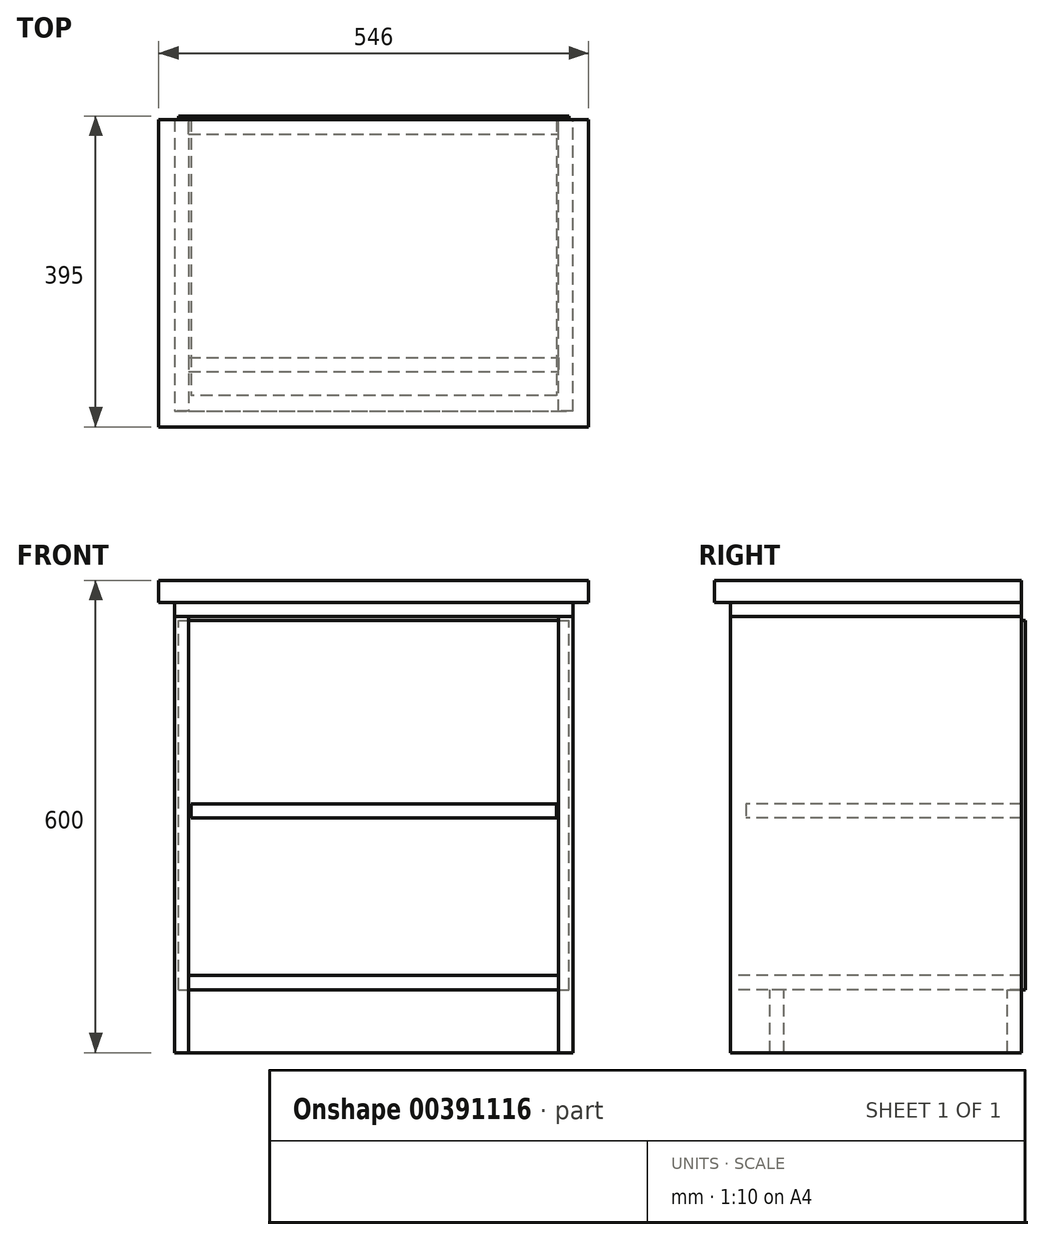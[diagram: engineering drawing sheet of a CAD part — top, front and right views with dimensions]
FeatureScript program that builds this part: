
annotation { "Feature Type Name" : "Feature", "Feature Type Description" : "" }
export const myFeature = defineFeature(function(context is Context, id is Id, definition is map)
    precondition{}
    {
        {
            assignVariable(context, id + "F0", {"name" : "ThickWood", "anyValue" : 28 * mm});
        }
        {
            assignVariable(context, id + "F1", {"name" : "WoodThickness", "anyValue" : 18 * mm});
        }
        {
            var Q0;
            Q0=qCreatedBy(makeId("Right.planeOp"),FACE);
            var sketch = newSketch(context, id + "F2", { "sketchPlane" : qUnion([Q0])});
            skLineSegment(sketch, "E0.bottom", {"start": v(0, 0) * mm, "end": v(-370, 0) * mm});
            skLineSegment(sketch, "E0.top", {"start": v(0, 554) * mm, "end": v(-370, 554) * mm});
            skLineSegment(sketch, "E0.left", {"start": v(0, 0) * mm, "end": v(0, 554) * mm});
            skLineSegment(sketch, "E0.right", {"start": v(-370, 0) * mm, "end": v(-370, 554) * mm});
            skSolve(sketch);
        }
        {
            var Q0;
            Q0=makeQuery(id+"F2.imprint","IMPRINT",FACE,{"disambiguationData":[TD([[makeQuery(id+"F2.imprint","IMPRINT",EDGE,{"derivedFrom":sQuery(id+"F2.wireOp",EDGE,"E0.bottom")}),-1.0]])]});
            extrude(context, id + "F3", {"entities" : qUnion([Q0]), "depth" : getVariable(context, 'WoodThickness')});
        }
        {
            var Q0;
            Q0=makeQuery(id+"F3.opExtrude","CAP_FACE",FACE,{"disambiguationData":[OSD([sQuery(id+"F2.wireOp",EDGE,"E0.bottom"),sQuery(id+"F2.wireOp",EDGE,"E0.top"),sQuery(id+"F2.wireOp",EDGE,"E0.left"),sQuery(id+"F2.wireOp",EDGE,"E0.right")])],"isStart":false});
            cPlane(context, id + "F4", {"entities" : qUnion([Q0]), "cplaneType" : CPlaneType.OFFSET, "offset" : 470 * mm, "width" : 150 * mm, "height" : 150 * mm});
        }
        {
            var Q0;
            Q0=qCreatedBy(id+"F4.planeOp",FACE);
            var sketch = newSketch(context, id + "F5", { "sketchPlane" : qUnion([Q0])});
            skLineSegment(sketch, "E1.bottom", {"start": v(-370, 554) * mm, "end": v(0, 554) * mm});
            skLineSegment(sketch, "E1.top", {"start": v(-370, 0) * mm, "end": v(0, 0) * mm});
            skLineSegment(sketch, "E1.left", {"start": v(-370, 554) * mm, "end": v(-370, 0) * mm});
            skLineSegment(sketch, "E1.right", {"start": v(0, 554) * mm, "end": v(0, 0) * mm});
            skSolve(sketch);
        }
        {
            var Q0;
            Q0=makeQuery(id+"F5.imprint","IMPRINT",FACE,{"disambiguationData":[TD([[makeQuery(id+"F5.imprint","IMPRINT",EDGE,{"derivedFrom":sQuery(id+"F5.wireOp",EDGE,"E1.bottom")}),-1.0]])]});
            extrude(context, id + "F6", {"entities" : qUnion([Q0]), "depth" : getVariable(context, 'WoodThickness')});
        }
        {
            assignVariable(context, id + "F7", {"name" : "ToeKickDepth", "anyValue" : 50 * mm});
        }
        {
            var Q0;
            Q0=makeQuery(id+"F3.opExtrude","SWEPT_FACE",FACE,{"disambiguationData":[OSD([sQuery(id+"F2.wireOp",EDGE,"E0.right")])]});
            cPlane(context, id + "F8", {"entities" : qUnion([Q0]), "cplaneType" : CPlaneType.OFFSET, "offset" : getVariable(context, 'ToeKickDepth'), "oppositeDirection" : true, "width" : 150 * mm, "height" : 150 * mm});
        }
        {
            var Q0;
            Q0=qCreatedBy(id+"F8.planeOp",FACE);
            var sketch = newSketch(context, id + "F9", { "sketchPlane" : qUnion([Q0])});
            skLineSegment(sketch, "E2.bottom", {"start": v(18, 0) * mm, "end": v(488, 0) * mm});
            skLineSegment(sketch, "E2.top", {"start": v(18, 80) * mm, "end": v(488, 80) * mm});
            skLineSegment(sketch, "E2.left", {"start": v(18, 0) * mm, "end": v(18, 80) * mm});
            skLineSegment(sketch, "E2.right", {"start": v(488, 0) * mm, "end": v(488, 80) * mm});
            skSolve(sketch);
        }
        {
            var Q0;
            Q0=makeQuery(id+"F9.imprint","IMPRINT",FACE,{"disambiguationData":[TD([[makeQuery(id+"F9.imprint","IMPRINT",EDGE,{"derivedFrom":sQuery(id+"F9.wireOp",EDGE,"E2.bottom")}),1.0]])]});
            extrude(context, id + "F10", {"entities" : qUnion([Q0]), "oppositeDirection" : true, "depth" : getVariable(context, 'WoodThickness')});
        }
        {
            var Q0;
            Q0=makeQuery(id+"F6.opExtrude","SWEPT_FACE",FACE,{"disambiguationData":[OSD([sQuery(id+"F5.wireOp",EDGE,"E1.right")])]});
            var sketch = newSketch(context, id + "F11", { "sketchPlane" : qUnion([Q0])});
            skLineSegment(sketch, "E3.0.0", {"start": v(-18, 80) * mm, "end": v(-488, 80) * mm});
            skLineSegment(sketch, "E3.0.1", {"start": v(-488, 80) * mm, "end": v(-488, 0) * mm});
            skLineSegment(sketch, "E3.0.2", {"start": v(-488, 0) * mm, "end": v(-18, 0) * mm});
            skLineSegment(sketch, "E3.0.3", {"start": v(-18, 0) * mm, "end": v(-18, 80) * mm});
            skSolve(sketch);
        }
        {
            var Q0;
            Q0=makeQuery(id+"F11.imprint","IMPRINT",FACE,{"disambiguationData":[TD([[makeQuery(id+"F11.imprint","IMPRINT",EDGE,{"derivedFrom":sQuery(id+"F11.wireOp",EDGE,"E3.0.0")}),1.0]])]});
            extrude(context, id + "F12", {"entities" : qUnion([Q0]), "oppositeDirection" : true, "depth" : getVariable(context, 'WoodThickness')});
        }
        {
            var Q0;
            Q0=makeQuery(id+"F12.opExtrude","SWEPT_FACE",FACE,{"disambiguationData":[OSD([sQuery(id+"F11.wireOp",EDGE,"E3.0.0")])]});
            var sketch = newSketch(context, id + "F13", { "sketchPlane" : qUnion([Q0])});
            skLineSegment(sketch, "E4.bottom", {"start": v(18, 0) * mm, "end": v(488, 0) * mm});
            skLineSegment(sketch, "E4.top", {"start": v(18, -370) * mm, "end": v(488, -370) * mm});
            skLineSegment(sketch, "E4.left", {"start": v(18, 0) * mm, "end": v(18, -370) * mm});
            skLineSegment(sketch, "E4.right", {"start": v(488, 0) * mm, "end": v(488, -370) * mm});
            skSolve(sketch);
        }
        {
            var Q0;
            {var subQ0=sQuery(id+"F13.wireOp",EDGE,"E4.top");Q0=makeQuery(id+"F13.imprint","IMPRINT",FACE,{"disambiguationData":[TD([[makeQuery(id+"F13.imprint","IMPRINT",EDGE,{"derivedFrom":subQ0}),1.0]])]});}
            var Q1;
            {var subQ0=sQuery(id+"F13.wireOp",EDGE,"E4.bottom");Q1=makeQuery(id+"F13.imprint","IMPRINT",FACE,{"disambiguationData":[TD([[makeQuery(id+"F13.imprint","IMPRINT",EDGE,{"derivedFrom":subQ0}),-1.0]])]});}
            extrude(context, id + "F14", {"entities" : qUnion([Q0, Q1]), "depth" : getVariable(context, 'WoodThickness')});
        }
        {
            var Q0;
            Q0=makeQuery(id+"F3.opExtrude","SWEPT_FACE",FACE,{"disambiguationData":[OSD([sQuery(id+"F2.wireOp",EDGE,"E0.top")])]});
            var sketch = newSketch(context, id + "F15", { "sketchPlane" : qUnion([Q0])});
            skLineSegment(sketch, "E5.bottom", {"start": v(0, 0) * mm, "end": v(506, 0) * mm});
            skLineSegment(sketch, "E5.top", {"start": v(0, -370) * mm, "end": v(506, -370) * mm});
            skLineSegment(sketch, "E5.left", {"start": v(0, 0) * mm, "end": v(0, -370) * mm});
            skLineSegment(sketch, "E5.right", {"start": v(506, 0) * mm, "end": v(506, -370) * mm});
            skSolve(sketch);
        }
        {
            var Q0;
            {var subQ2=sQuery(id+"F15.wireOp",EDGE,"E5.right");Q0=makeQuery(id+"F15.imprint","IMPRINT",FACE,{"disambiguationData":[TD([[makeQuery(id+"F15.imprint","IMPRINT",EDGE,{"derivedFrom":subQ2}),-1.0]])]});}
            var Q1;
            {var subQ0=sQuery(id+"F15.wireOp",EDGE,"E5.left");Q1=makeQuery(id+"F15.imprint","IMPRINT",FACE,{"disambiguationData":[TD([[makeQuery(id+"F15.imprint","IMPRINT",EDGE,{"derivedFrom":subQ0}),1.0]])]});}
            extrude(context, id + "F16", {"entities" : qUnion([Q0, Q1]), "depth" : getVariable(context, 'WoodThickness')});
        }
        {
            var Q0;
            Q0=makeQuery(id+"F16.opExtrude","CAP_FACE",FACE,{"disambiguationData":[OSD([sQuery(id+"F15.wireOp",EDGE,"E5.bottom"),sQuery(id+"F15.wireOp",EDGE,"E5.top"),sQuery(id+"F15.wireOp",EDGE,"E5.left"),sQuery(id+"F15.wireOp",EDGE,"E5.right")])],"isStart":false});
            var sketch = newSketch(context, id + "F17", { "sketchPlane" : qUnion([Q0])});
            skLineSegment(sketch, "E6.bottom", {"start": v(-20, 0) * mm, "end": v(526, 0) * mm});
            skLineSegment(sketch, "E6.top", {"start": v(-20, -390) * mm, "end": v(526, -390) * mm});
            skLineSegment(sketch, "E6.left", {"start": v(-20, 0) * mm, "end": v(-20, -390) * mm});
            skLineSegment(sketch, "E6.right", {"start": v(526, 0) * mm, "end": v(526, -390) * mm});
            skSolve(sketch);
        }
        {
            var Q0;
            Q0=makeQuery(id+"F17.imprint","IMPRINT",FACE,{"disambiguationData":[TD([[makeQuery(id+"F17.imprint","IMPRINT",EDGE,{"derivedFrom":makeQuery(id+"F16.opExtrude","CAP_EDGE",EDGE,{"disambiguationData":[OSD([sQuery(id+"F15.wireOp",EDGE,"E5.top")])],"isStart":false})}),1.0]])]});
            var Q1;
            Q1=makeQuery(id+"F17.imprint","IMPRINT",FACE,{"disambiguationData":[TD([[makeQuery(id+"F17.imprint","IMPRINT",EDGE,{"derivedFrom":sQuery(id+"F17.wireOp",EDGE,"E6.top")}),1.0]])]});
            extrude(context, id + "F18", {"entities" : qUnion([Q0, Q1]), "depth" : getVariable(context, 'ThickWood')});
        }
        {
            var Q0;
            Q0=makeQuery(id+"F14.opExtrude","CAP_FACE",FACE,{"disambiguationData":[OSD([sQuery(id+"F13.wireOp",EDGE,"E4.bottom"),sQuery(id+"F13.wireOp",EDGE,"E4.top"),sQuery(id+"F13.wireOp",EDGE,"E4.left"),sQuery(id+"F13.wireOp",EDGE,"E4.right")])],"isStart":false});
            cPlane(context, id + "F19", {"entities" : qUnion([Q0]), "cplaneType" : CPlaneType.OFFSET, "offset" : 200 * mm, "width" : 150 * mm, "height" : 150 * mm});
        }
        {
            var Q0;
            Q0=qCreatedBy(id+"F19.planeOp",FACE);
            var sketch = newSketch(context, id + "F20", { "sketchPlane" : qUnion([Q0])});
            skLineSegment(sketch, "E7.bottom", {"start": v(485, 0) * mm, "end": v(21, 0) * mm});
            skLineSegment(sketch, "E7.top", {"start": v(485, -350) * mm, "end": v(21, -350) * mm});
            skLineSegment(sketch, "E7.left", {"start": v(485, 0) * mm, "end": v(485, -350) * mm});
            skLineSegment(sketch, "E7.right", {"start": v(21, 0) * mm, "end": v(21, -350) * mm});
            skSolve(sketch);
        }
        {
            var Q0;
            Q0=makeQuery(id+"F20.imprint","IMPRINT",FACE,{"disambiguationData":[TD([[makeQuery(id+"F20.imprint","IMPRINT",EDGE,{"derivedFrom":sQuery(id+"F20.wireOp",EDGE,"E7.bottom")}),1.0]])]});
            extrude(context, id + "F21", {"entities" : qUnion([Q0]), "depth" : getVariable(context, 'WoodThickness')});
        }
        {
            assignVariable(context, id + "F22", {"name" : "BackingThickness", "anyValue" : 5 * mm});
        }
        {
            var Q0;
            Q0=makeQuery(id+"F3.opExtrude","SWEPT_FACE",FACE,{"disambiguationData":[OSD([sQuery(id+"F2.wireOp",EDGE,"E0.left")])]});
            var sketch = newSketch(context, id + "F23", { "sketchPlane" : qUnion([Q0])});
            skLineSegment(sketch, "E8.bottom", {"start": v(-5, 80) * mm, "end": v(-501, 80) * mm});
            skLineSegment(sketch, "E8.top", {"start": v(-5, 549) * mm, "end": v(-501, 549) * mm});
            skLineSegment(sketch, "E8.left", {"start": v(-5, 80) * mm, "end": v(-5, 549) * mm});
            skLineSegment(sketch, "E8.right", {"start": v(-501, 80) * mm, "end": v(-501, 549) * mm});
            skSolve(sketch);
        }
        {
            var Q0;
            {var subQ4=sQuery(id+"F23.wireOp",EDGE,"E8.top");Q0=makeQuery(id+"F23.imprint","IMPRINT",FACE,{"disambiguationData":[TD([[makeQuery(id+"F23.imprint","IMPRINT",EDGE,{"derivedFrom":subQ4}),1.0]])]});}
            extrude(context, id + "F24", {"entities" : qUnion([Q0]), "depth" : getVariable(context, 'BackingThickness')});
        }
    });
